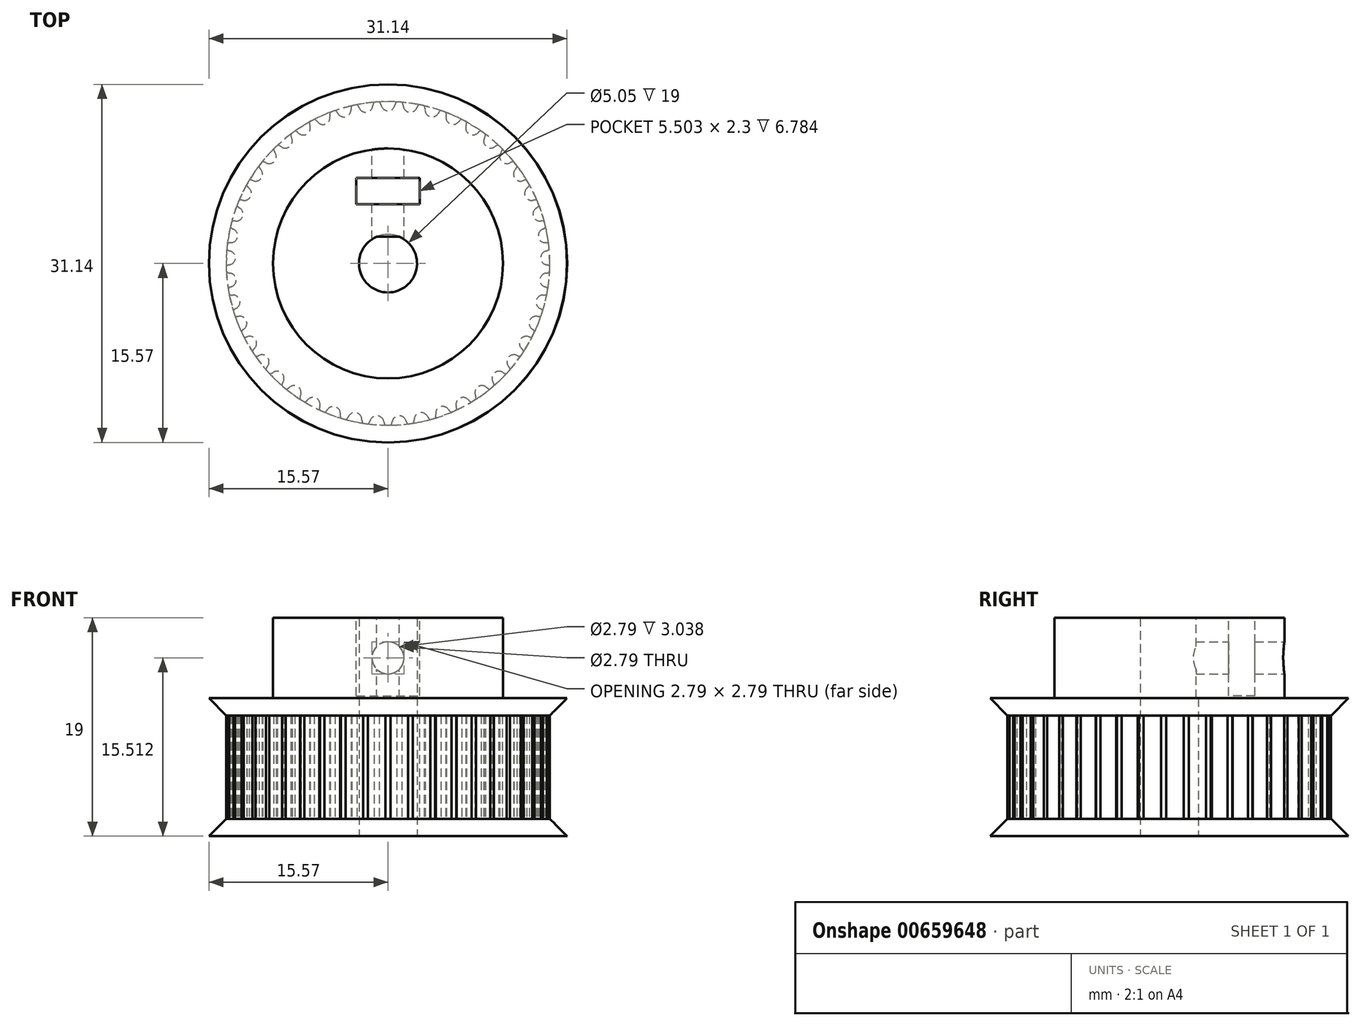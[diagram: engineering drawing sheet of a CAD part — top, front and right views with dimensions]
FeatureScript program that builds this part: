
annotation { "Feature Type Name" : "Feature", "Feature Type Description" : "" }
export const myFeature = defineFeature(function(context is Context, id is Id, definition is map)
    precondition{}
    {
        {
            assignVariable(context, id + "F0", {"name" : "Teeth", "anyValue" : 45});
        }
        {
            var Q0;
            Q0=qCreatedBy(makeId("Top.planeOp"),FACE);
            var sketch = newSketch(context, id + "F1", { "sketchPlane" : qUnion([Q0])});
            skCircle(sketch, "E0", {"center": v(0, 0) * mm, "radius": 14.07 * mm});
            skSolve(sketch);
        }
        {
            var Q0;
            Q0=qCreatedBy(makeId("Top.planeOp"),FACE);
            var sketch = newSketch(context, id + "F2", { "sketchPlane" : qUnion([Q0])});
            skArc(sketch, "E1.0", {"start": v(0.77, 14.05) * mm, "mid": v(0, 14.07) * mm, "end": v(-0.77, 14.05) * mm});
            skLineSegment(sketch, "E2", {"start": v(0, 0) * mm, "end": v(0, 13.9) * mm, "construction": true});
            skArc(sketch, "E3", {"start": v(0, 13.28) * mm, "mid": v(-0.38, 13.42) * mm, "end": v(-0.6, 13.76) * mm});
            skArc(sketch, "E4", {"start": v(-0.6, 13.76) * mm, "mid": v(-0.63, 13.87) * mm, "end": v(-0.68, 13.96) * mm});
            skArc(sketch, "E5", {"start": v(-0.68, 13.96) * mm, "mid": v(-0.71, 14.01) * mm, "end": v(-0.77, 14.05) * mm});
            skArc(sketch, "E6.MirrorCS", {"start": v(0, 13.28) * mm, "mid": v(0.38, 13.42) * mm, "end": v(0.6, 13.76) * mm});
            skArc(sketch, "E7.MirrorCS", {"start": v(0.68, 13.96) * mm, "mid": v(0.71, 14.01) * mm, "end": v(0.77, 14.05) * mm});
            skArc(sketch, "E8.MirrorCS", {"start": v(0.6, 13.76) * mm, "mid": v(0.63, 13.87) * mm, "end": v(0.68, 13.96) * mm});
            skSolve(sketch);
        }
        {
            var Q0;
            Q0=qSketchRegion(id+"F1",true);
            extrude(context, id + "F3", {"entities" : qUnion([Q0]), "depth" : 9 * mm, "offsetDistance" : 25 * mm});
        }
        {
            var Q0;
            Q0=makeQuery(id+"F2.imprint","IMPRINT",FACE,{"disambiguationData":[TD([[makeQuery(id+"F2.imprint","IMPRINT",EDGE,{"derivedFrom":sQuery(id+"F2.wireOp",EDGE,"E1.0")}),1.0]])]});
            extrude(context, id + "F4", {"entities" : qUnion([Q0]), "depth" : 25 * mm, "offsetDistance" : 25 * mm});
        }
        {
            var Q0;
            Q0=makeQuery(id+"F4.opExtrude","SWEPT_BODY",BODY,{"disambiguationData":[OSD([sQuery(id+"F2.wireOp",EDGE,"E1.0"),sQuery(id+"F2.wireOp",EDGE,"E3"),sQuery(id+"F2.wireOp",EDGE,"E4"),sQuery(id+"F2.wireOp",EDGE,"E5"),sQuery(id+"F2.wireOp",EDGE,"E6.MirrorCS"),sQuery(id+"F2.wireOp",EDGE,"E7.MirrorCS"),sQuery(id+"F2.wireOp",EDGE,"E8.MirrorCS")])]});
            var Q1;
            Q1=sQuery(id+"F1.wireOp",EDGE,"E0");
            circularPattern(context, id + "F5", {"operationType" : NewBodyOperationType.REMOVE, "entities" : qUnion([Q0]), "axis" : qUnion([Q1]), "angle" : 360 * degree, "instanceCount" : getVariable(context, 'Teeth'), "equalSpace" : true});
        }
        {
            var Q0;
            Q0=makeQuery(id+"F3.opExtrude","CAP_FACE",FACE,{"disambiguationData":[OSD([sQuery(id+"F1.wireOp",EDGE,"E0")])],"isStart":false});
            var sketch = newSketch(context, id + "F6", { "sketchPlane" : qUnion([Q0])});
            skCircle(sketch, "E9", {"center": v(0, 0) * mm, "radius": 10 * mm});
            skSolve(sketch);
        }
        {
            var Q0;
            Q0=makeQuery(id+"F6.imprint","IMPRINT",FACE,{"disambiguationData":[TD([[makeQuery(id+"F6.imprint","IMPRINT",EDGE,{"derivedFrom":sQuery(id+"F6.wireOp",EDGE,"E9")}),-1.0]])]});
            var sketch = newSketch(context, id + "F7", { "sketchPlane" : qUnion([Q0])});
            skCircle(sketch, "E10.0", {"center": v(0, 0) * mm, "radius": 14.07 * mm});
            skSolve(sketch);
        }
        {
            var Q0;
            Q0 = qSketchRegion(id + "F7", true);
            extrude(context, id + "F8", {"entities" : qUnion([Q0]), "operationType" : NewBodyOperationType.ADD, "depth" : 1.5 * mm, "offsetDistance" : 25 * mm, "hasDraft" : true, "draftAngle" : 45 * degree});
        }
        {
            var Q0;
            Q0=qSketchRegion(id+"F6",true);
            extrude(context, id + "F9", {"entities" : qUnion([Q0]), "operationType" : NewBodyOperationType.ADD, "depth" : 8.5 * mm, "offsetDistance" : 25 * mm});
        }
        {
            var Q0;
            Q0=qCreatedBy(makeId("Top.planeOp"),FACE);
            var sketch = newSketch(context, id + "F10", { "sketchPlane" : qUnion([Q0])});
            skCircle(sketch, "E11", {"center": v(0, 0) * mm, "radius": 2.52 * mm});
            skSolve(sketch);
        }
        {
            var Q0;
            Q0=qCreatedBy(makeId("Top.planeOp"),FACE);
            var sketch = newSketch(context, id + "F11", { "sketchPlane" : qUnion([Q0])});
            skCircle(sketch, "E12.0", {"center": v(0, 0) * mm, "radius": 2.6 * mm});
            skSolve(sketch);
        }
        {
            var Q0;
            Q0=makeQuery(id+"F9.opExtrude","CAP_FACE",FACE,{"disambiguationData":[OSD([sQuery(id+"F6.wireOp",EDGE,"E9")])],"isStart":false});
            var sketch = newSketch(context, id + "F12", { "sketchPlane" : qUnion([Q0])});
            skLineSegment(sketch, "E13", {"start": v(0, 10) * mm, "end": v(0, 7.44) * mm, "construction": true});
            skLineSegment(sketch, "E14.bottom", {"start": v(-2.75, 7.44) * mm, "end": v(2.75, 7.44) * mm});
            skLineSegment(sketch, "E14.top", {"start": v(-2.75, 7.44) * mm, "end": v(2.75, 7.44) * mm});
            skLineSegment(sketch, "E14.left", {"start": v(-2.75, 7.44) * mm, "end": v(-2.75, 7.44) * mm});
            skLineSegment(sketch, "E14.right", {"start": v(2.75, 7.44) * mm, "end": v(2.75, 7.44) * mm});
            skPoint(sketch, "E14.middle", {"position": v(0, 7.44) * mm});
            skLineSegment(sketch, "E15.top", {"start": v(-2.75, 5.14) * mm, "end": v(2.75, 5.14) * mm});
            skLineSegment(sketch, "E15.left", {"start": v(-2.75, 7.44) * mm, "end": v(-2.75, 5.14) * mm});
            skLineSegment(sketch, "E15.right", {"start": v(2.75, 7.44) * mm, "end": v(2.75, 5.14) * mm});
            skSolve(sketch);
        }
        {
            var Q0;
            Q0=qSketchRegion(id+"F12",true);
            extrude(context, id + "F13", {"entities" : qUnion([Q0]), "operationType" : NewBodyOperationType.REMOVE, "oppositeDirection" : true, "depth" : 6.78 * mm, "offsetDistance" : 25 * mm});
        }
        {
            var Q0;
            Q0=makeQuery(id+"F13.boolean.opBoolean","COPY",FACE,{"derivedFrom":makeQuery(id+"F13.opExtrude","SWEPT_FACE",FACE,{"disambiguationData":[OSD([sQuery(id+"F12.wireOp",EDGE,"E15.top")])]})});
            var sketch = newSketch(context, id + "F14", { "sketchPlane" : qUnion([Q0])});
            skLineSegment(sketch, "E16", {"start": v(0, 17.5) * mm, "end": v(0, 15.4) * mm, "construction": true});
            skLineSegment(sketch, "E17", {"start": v(0, 15.4) * mm, "end": v(0, 12.62) * mm, "construction": true});
            skCircle(sketch, "E18", {"center": v(0, 14.01) * mm, "radius": 1.4 * mm});
            skSolve(sketch);
        }
        {
            var Q0;
            Q0=makeQuery(id+"F11.imprint","IMPRINT",FACE,{"disambiguationData":[TD([[makeQuery(id+"F11.imprint","IMPRINT",EDGE,{"derivedFrom":sQuery(id+"F11.wireOp",EDGE,"E12.0")}),1.0]])]});
            var sketch = newSketch(context, id + "F15", { "sketchPlane" : qUnion([Q0])});
            skCircle(sketch, "E19", {"center": v(0, 0) * mm, "radius": 14.07 * mm});
            skSolve(sketch);
        }
        {
            var Q0;
            Q0 = qSketchRegion(id + "F15", true);
            extrude(context, id + "F16", {"entities" : qUnion([Q0]), "operationType" : NewBodyOperationType.ADD, "oppositeDirection" : true, "depth" : 1.5 * mm, "offsetDistance" : 25 * mm, "hasDraft" : true, "draftAngle" : 45 * degree});
        }
        {
            var Q0;
            Q0=qSketchRegion(id+"F10",true);
            var Q1;
            Q1=sQuery(id+"F10.wireOp",EDGE,"E11");
            extrude(context, id + "F17", {"entities" : qUnion([Q0]), "operationType" : NewBodyOperationType.REMOVE, "surfaceEntities" : qUnion([Q1]), "depth" : 25 * mm, "offsetDistance" : 25 * mm, "hasSecondDirection" : true, "secondDirectionOppositeDirection" : true, "secondDirectionDepth" : 25 * mm});
        }
        {
            var Q0;
            Q0=makeQuery(id+"F9.opExtrude","CAP_FACE",FACE,{"disambiguationData":[OSD([sQuery(id+"F6.wireOp",EDGE,"E9")])],"isStart":false});
            var sketch = newSketch(context, id + "F18", { "sketchPlane" : qUnion([Q0])});
            skCircle(sketch, "E20", {"center": v(0, 0) * mm, "radius": 2.33 * mm, "construction": true});
            skCircle(sketch, "E21.0", {"center": v(0, 0) * mm, "radius": 2.52 * mm, "construction": true});
            skArc(sketch, "E22", {"start": v(0, -2.52) * mm, "mid": v(0.5, 2.47) * mm, "end": v(-0.98, -2.33) * mm});
            skLineSegment(sketch, "E23", {"start": v(0, 2.33) * mm, "end": v(-0.98, 2.33) * mm});
            skLineSegment(sketch, "E24", {"start": v(0, 2.33) * mm, "end": v(0.98, 2.33) * mm});
            skArc(sketch, "E25", {"start": v(-0.98, 2.32) * mm, "mid": v(0.5, -2.47) * mm, "end": v(0, 2.52) * mm});
            skSolve(sketch);
        }
        {
            var Q0;
            {var subQ0=sQuery(id+"F18.wireOp",EDGE,"E22");Q0=makeQuery(id+"F18.imprint","IMPRINT",FACE,{"disambiguationData":[TD([[makeQuery(id+"F18.imprint","IMPRINT",EDGE,{"derivedFrom":subQ0}),-1.0]])]});}
            var Q1;
            Q1=makeQuery(id+"F8.opExtrude","CAP_FACE",FACE,{"disambiguationData":[OSD([sQuery(id+"F7.wireOp",EDGE,"E10.0")])],"isStart":false});
            var Q2;
            Q2=makeQuery(id+"F16.opExtrude","CAP_FACE",FACE,{"disambiguationData":[OSD([sQuery(id+"F15.wireOp",EDGE,"E19")])],"isStart":false});
            extrude(context, id + "F19", {"entities" : qUnion([Q0]), "operationType" : NewBodyOperationType.ADD, "endBound" : BoundingType.UP_TO_SURFACE, "oppositeDirection" : true, "depth" : 25 * mm, "endBoundEntityFace" : qUnion([Q1]), "offsetDistance" : 5 * mm});
        }
        {
            var Q0;
            Q0=makeQuery(id+"F14.imprint","IMPRINT",FACE,{"disambiguationData":[TD([[makeQuery(id+"F14.imprint","IMPRINT",EDGE,{"derivedFrom":sQuery(id+"F14.wireOp",EDGE,"E18")}),1.0]])]});
            extrude(context, id + "F20", {"entities" : qUnion([Q0]), "operationType" : NewBodyOperationType.REMOVE, "oppositeDirection" : true, "depth" : 5 * mm, "offsetDistance" : 25 * mm, "hasSecondDirection" : true, "secondDirectionOppositeDirection" : false, "secondDirectionDepth" : 15 * mm});
        }
    });
